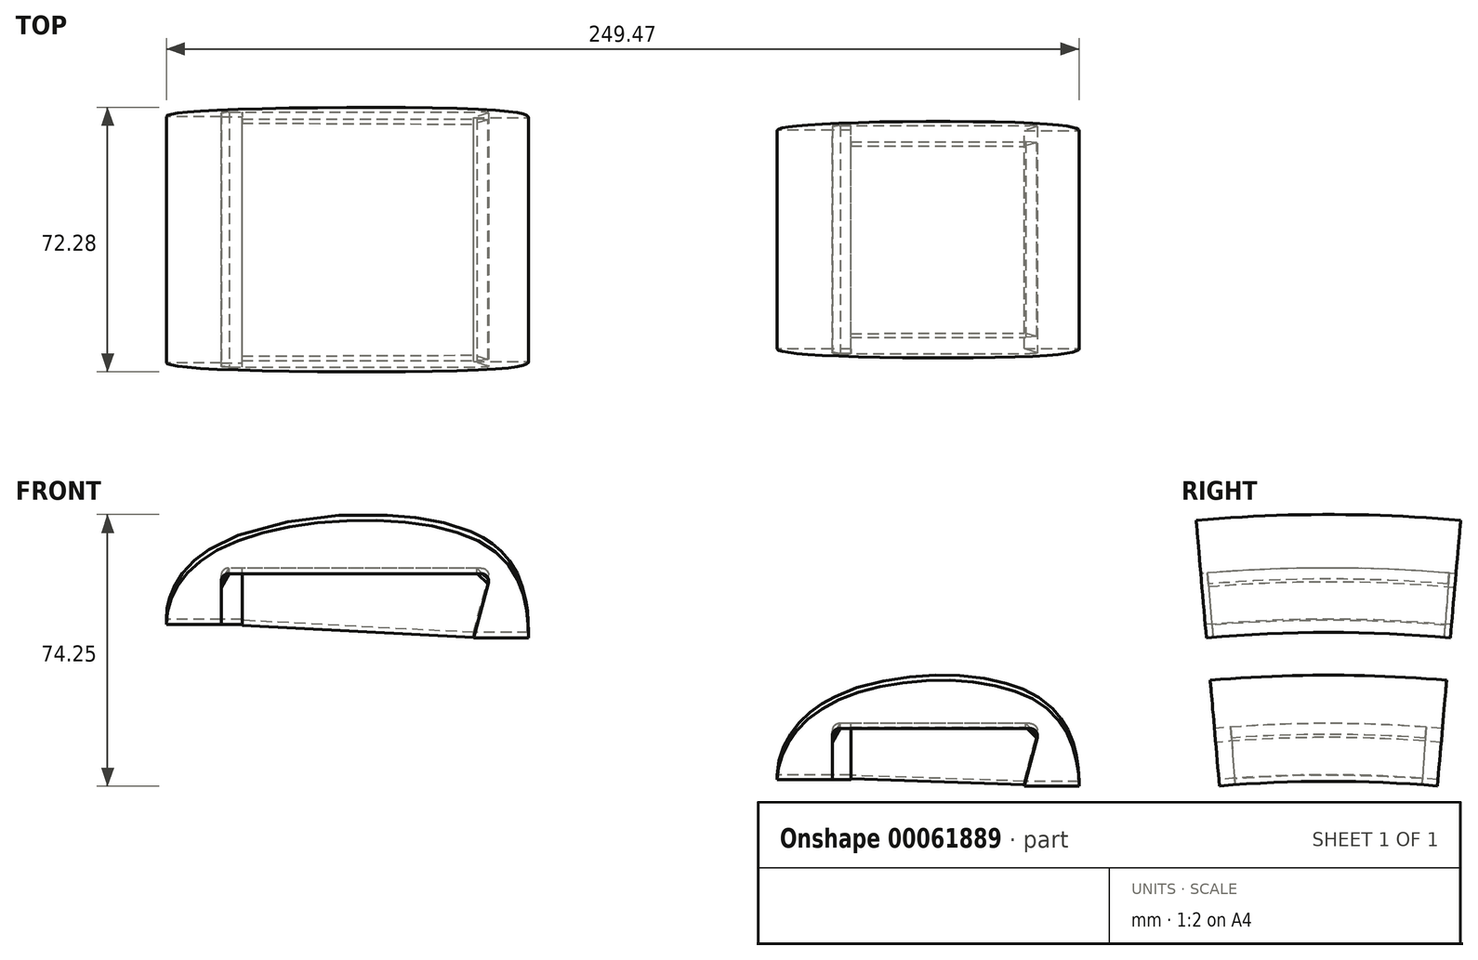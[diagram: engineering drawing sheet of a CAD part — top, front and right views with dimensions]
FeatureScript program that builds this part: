
annotation { "Feature Type Name" : "Feature", "Feature Type Description" : "" }
export const myFeature = defineFeature(function(context is Context, id is Id, definition is map)
    precondition{}
    {
        {
            assignVariable(context, id + "F0", {"name" : "C", "anyValue" : 2.2});
        }
        {
            assignVariable(context, id + "F1", {"name" : "Rev", "anyValue" : 10});
        }
        {
            assignVariable(context, id + "F2", {"name" : "a7", "anyValue" : 360 / 42});
        }
        {
            assignVariable(context, id + "F3", {"name" : "a1", "anyValue" : 360 / 38});
        }
        {
            var Q0;
            Q0=qCreatedBy(makeId("Front.planeOp"),FACE);
            var sketch = newSketch(context, id + "F4", { "sketchPlane" : qUnion([Q0])});
            skLineSegment(sketch, "E0", {"start": v(-50, 0) * mm, "end": v(50, 0) * mm, "construction": true});
            skSolve(sketch);
        }
        {
            var Q0;
            Q0=qCreatedBy(makeId("Front.planeOp"),FACE);
            var sketch = newSketch(context, id + "F5", { "sketchPlane" : qUnion([Q0])});
            skLineSegment(sketch, "E1", {"start": v(93.3, 357.5) * mm, "end": v(150, 357.5) * mm});
            skLineSegment(sketch, "E2", {"start": v(93.3, 357.5) * mm, "end": v(93.3, 343.5) * mm});
            skLineSegment(sketch, "E3", {"start": v(150, 357.5) * mm, "end": v(145.77, 341.7) * mm});
            skLineSegment(sketch, "E4", {"start": v(145.77, 341.7) * mm, "end": v(160.77, 341.7) * mm});
            skLineSegment(sketch, "E5", {"start": v(93.3, 343.5) * mm, "end": v(78.3, 343.5) * mm});
            skPoint(sketch, "E6.visualSharp", {"position": v(150, 357.5) * mm});
            skLineSegment(sketch, "E7", {"start": v(93.3, 343.5) * mm, "end": v(145.77, 341.7) * mm});
            skFitSpline(sketch, "E8", {"points": [v(78.3, 343.5) * mm, v(93.3, 364.5) * mm, v(150, 364.5) * mm, v(160.77, 341.7) * mm], "startDerivative": vector(0, 72.88) * mm, "endDerivative": vector(0, -73.74) * mm});
            skLineSegment(sketch, "E9", {"start": v(98.4, 357.5) * mm, "end": v(98.4, 343.33) * mm});
            skSolve(sketch);
        }
        {
            var Q0;
            Q0=qCreatedBy(makeId("Front.planeOp"),FACE);
            var sketch = newSketch(context, id + "F6", { "sketchPlane" : qUnion([Q0])});
            skLineSegment(sketch, "E10.top", {"start": v(98.4, 343.5) * mm, "end": v(93.3, 343.5) * mm});
            skLineSegment(sketch, "E10.right", {"start": v(93.3, 357.5) * mm, "end": v(93.3, 343.5) * mm});
            skLineSegment(sketch, "E11", {"start": v(98.4, 343.5) * mm, "end": v(98.4, 357.5) * mm});
            skLineSegment(sketch, "E12", {"start": v(98.4, 357.5) * mm, "end": v(93.3, 357.5) * mm});
            skSolve(sketch);
        }
        {
            var Q0;
            Q0=qCreatedBy(makeId("Front.planeOp"),FACE);
            var sketch = newSketch(context, id + "F7", { "sketchPlane" : qUnion([Q0])});
            skLineSegment(sketch, "E13", {"start": v(-73.7, 400) * mm, "end": v(0, 400) * mm});
            skLineSegment(sketch, "E14", {"start": v(0, 400) * mm, "end": v(-4.72, 382.38) * mm});
            skLineSegment(sketch, "E15", {"start": v(-73.7, 386) * mm, "end": v(-88.7, 386) * mm});
            skPoint(sketch, "E16.visualSharp", {"position": v(0, 400) * mm});
            skLineSegment(sketch, "E17", {"start": v(-73.7, 386) * mm, "end": v(-73.7, 400) * mm});
            skLineSegment(sketch, "E18", {"start": v(-73.7, 386) * mm, "end": v(-4.72, 382.38) * mm});
            skLineSegment(sketch, "E19", {"start": v(-4.72, 382.38) * mm, "end": v(10.28, 382.38) * mm});
            skFitSpline(sketch, "E20", {"points": [v(-88.7, 386) * mm, v(-73.7, 407) * mm, v(0, 407) * mm, v(10.28, 382.38) * mm], "startDerivative": vector(0, 77.84) * mm, "endDerivative": vector(0, -76.56) * mm});
            skLineSegment(sketch, "E21", {"start": v(-68, 400) * mm, "end": v(-68, 385.7) * mm});
            skSolve(sketch);
        }
        {
            var Q0;
            Q0=qCreatedBy(makeId("Front.planeOp"),FACE);
            var sketch = newSketch(context, id + "F8", { "sketchPlane" : qUnion([Q0])});
            skLineSegment(sketch, "E22.bottom", {"start": v(-73.7, 400) * mm, "end": v(-68, 400) * mm});
            skLineSegment(sketch, "E22.top", {"start": v(-73.7, 386) * mm, "end": v(-68, 386) * mm});
            skLineSegment(sketch, "E22.left", {"start": v(-73.7, 400) * mm, "end": v(-73.7, 386) * mm});
            skLineSegment(sketch, "E22.right", {"start": v(-68, 400) * mm, "end": v(-68, 386) * mm});
            skSolve(sketch);
        }
        {
            var Q0;
            Q0 = qSketchRegion(id + "F6", true);
            var Q1;
            Q1=sQuery(id+"F4.wireOp",EDGE,"E0");
            revolve(context, id + "F9", {"entities" : qUnion([Q0]), "axis" : qUnion([Q1]), "revolveType" : RevolveType.SYMMETRIC, "angle" : (getVariable(context, 'Rev')) * degree});
        }
        {
            var Q0;
            Q0=makeQuery(id+"F9.opRevolve","SWEPT_EDGE",EDGE,{"disambiguationData":[OSD([sQuery(id+"F6.wireOp",EDGE,"E10.right"),sQuery(id+"F6.wireOp",EDGE,"E12")])]});
            chamfer(context, id + "F10", {"entities" : qUnion([Q0]), "chamferType" : ChamferType.OFFSET_ANGLE, "width" : (getVariable(context, 'C')) * mm, "oppositeDirection" : true, "angle" : 60 * degree, "tangentPropagation" : true});
        }
        {
            var Q0;
            {var subQ1=sQuery(id+"F5.wireOp",EDGE,"E3");Q0=makeQuery(id+"F5.imprint","IMPRINT",FACE,{"disambiguationData":[TD([[makeQuery(id+"F5.imprint","IMPRINT",EDGE,{"derivedFrom":subQ1}),1.0]])]});}
            var Q1;
            {var subQ0=sQuery(id+"F5.wireOp",EDGE,"wodW1qH4-quOG-skXt-y23y-Nep1uXmpPe48");Q1=makeQuery(id+"F5.imprint","IMPRINT",FACE,{"disambiguationData":[TD([[makeQuery(id+"F5.imprint","IMPRINT",EDGE,{"derivedFrom":subQ0}),-1.0]])]});}
            var Q2;
            {var subQ0=sQuery(id+"F5.wireOp",EDGE,"E2");Q2=makeQuery(id+"F5.imprint","IMPRINT",FACE,{"disambiguationData":[TD([[makeQuery(id+"F5.imprint","IMPRINT",EDGE,{"derivedFrom":subQ0}),-1.0]])]});}
            var Q3;
            Q3=sQuery(id+"F4.wireOp",EDGE,"E0");
            revolve(context, id + "F11", {"entities" : qUnion([Q0, Q1, Q2]), "axis" : qUnion([Q3]), "revolveType" : RevolveType.SYMMETRIC, "angle" : 10 * degree});
        }
        {
            var Q0;
            {var subQ0=sQuery(id+"F5.wireOp",EDGE,"E3");Q0=makeQuery(id+"F5.imprint","IMPRINT",FACE,{"disambiguationData":[TD([[makeQuery(id+"F5.imprint","IMPRINT",EDGE,{"derivedFrom":subQ0}),-1.0]])]});}
            var Q1;
            Q1=sQuery(id+"F4.wireOp",EDGE,"E0");
            revolve(context, id + "F12", {"entities" : qUnion([Q0]), "axis" : qUnion([Q1]), "revolveType" : RevolveType.SYMMETRIC, "angle" : (getVariable(context, 'a7')) * degree});
        }
        {
            var Q0;
            Q0=makeQuery(id+"F12.opRevolve","SWEPT_EDGE",EDGE,{"disambiguationData":[OSD([sQuery(id+"F5.wireOp",EDGE,"E1"),sQuery(id+"F5.wireOp",EDGE,"E3")])]});
            chamfer(context, id + "F13", {"entities" : qUnion([Q0]), "chamferType" : ChamferType.OFFSET_ANGLE, "width" : 3.8 * mm, "oppositeDirection" : false, "angle" : 45 * degree, "tangentPropagation" : true});
        }
        {
            var Q0;
            Q0=makeQuery(id+"F11.opRevolve","SWEPT_EDGE",EDGE,{"disambiguationData":[OSD([sQuery(id+"F5.wireOp",EDGE,"E1"),sQuery(id+"F5.wireOp",EDGE,"E2")])]});
            var Q1;
            Q1=makeQuery(id+"F11.opRevolve","SWEPT_EDGE",EDGE,{"disambiguationData":[OSD([sQuery(id+"F5.wireOp",EDGE,"E1"),sQuery(id+"F5.wireOp",EDGE,"E3")])]});
            fillet(context, id + "F14", {"entities" : qUnion([Q0, Q1]), "radius" : 2 * mm, "tangentPropagation" : true, "allowEdgeOverflow" : false});
        }
        {
            var Q0;
            Q0=makeQuery(id+"F8.imprint","IMPRINT",FACE,{"disambiguationData":[TD([[makeQuery(id+"F8.imprint","IMPRINT",EDGE,{"derivedFrom":sQuery(id+"F8.wireOp",EDGE,"E22.bottom")}),-1.0]])]});
            var Q1;
            Q1=sQuery(id+"F4.wireOp",EDGE,"E0");
            revolve(context, id + "F15", {"entities" : qUnion([Q0]), "axis" : qUnion([Q1]), "revolveType" : RevolveType.SYMMETRIC, "angle" : (getVariable(context, 'Rev')) * degree});
        }
        {
            var Q0;
            {var subQ0=sQuery(id+"F7.wireOp",EDGE,"E14");Q0=makeQuery(id+"F7.imprint","IMPRINT",FACE,{"disambiguationData":[TD([[makeQuery(id+"F7.imprint","IMPRINT",EDGE,{"derivedFrom":subQ0}),1.0]])]});}
            var Q1;
            Q1=sQuery(id+"F4.wireOp",EDGE,"E0");
            revolve(context, id + "F16", {"entities" : qUnion([Q0]), "axis" : qUnion([Q1]), "revolveType" : RevolveType.SYMMETRIC, "angle" : 10 * degree});
        }
        {
            var Q0;
            {var subQ0=sQuery(id+"F7.wireOp",EDGE,"E14");Q0=makeQuery(id+"F7.imprint","IMPRINT",FACE,{"disambiguationData":[TD([[makeQuery(id+"F7.imprint","IMPRINT",EDGE,{"derivedFrom":subQ0}),-1.0]])]});}
            var Q1;
            Q1=sQuery(id+"F4.wireOp",EDGE,"E0");
            revolve(context, id + "F17", {"entities" : qUnion([Q0]), "axis" : qUnion([Q1]), "revolveType" : RevolveType.SYMMETRIC, "angle" : (getVariable(context, 'a1')) * degree});
        }
        {
            var Q0;
            Q0=makeQuery(id+"F15.opRevolve","SWEPT_EDGE",EDGE,{"disambiguationData":[OSD([sQuery(id+"F8.wireOp",EDGE,"E22.bottom"),sQuery(id+"F8.wireOp",EDGE,"E22.left")])]});
            chamfer(context, id + "F18", {"entities" : qUnion([Q0]), "chamferType" : ChamferType.OFFSET_ANGLE, "width" : (getVariable(context, 'C')) * mm, "oppositeDirection" : true, "angle" : 60 * degree, "tangentPropagation" : true});
        }
        {
            var Q0;
            Q0=makeQuery(id+"F17.opRevolve","SWEPT_EDGE",EDGE,{"disambiguationData":[OSD([sQuery(id+"F7.wireOp",EDGE,"E13"),sQuery(id+"F7.wireOp",EDGE,"E14")])]});
            chamfer(context, id + "F19", {"entities" : qUnion([Q0]), "chamferType" : ChamferType.OFFSET_ANGLE, "width" : 3.8 * mm, "oppositeDirection" : false, "angle" : 45 * degree, "tangentPropagation" : true});
        }
        {
            var Q0;
            Q0=makeQuery(id+"F16.opRevolve","SWEPT_EDGE",EDGE,{"disambiguationData":[OSD([sQuery(id+"F7.wireOp",EDGE,"E13"),sQuery(id+"F7.wireOp",EDGE,"E14")])]});
            var Q1;
            Q1=makeQuery(id+"F16.opRevolve","SWEPT_EDGE",EDGE,{"disambiguationData":[OSD([sQuery(id+"F7.wireOp",EDGE,"E13"),sQuery(id+"F7.wireOp",EDGE,"E17")])]});
            fillet(context, id + "F20", {"entities" : qUnion([Q0, Q1]), "radius" : 2 * mm, "tangentPropagation" : true, "allowEdgeOverflow" : false});
        }
    });
